# Revit family: LMNE-VL
name_source: partatom
category: Lighting Fixtures
units: mm (PartAtom-declared; Revit-internal decimal feet)

## family parameters
Always vertical = Yes
Cut with Voids When Loaded = No
Host = Ceiling
Light Source = Yes
OmniClass Number = 23.80.70.11.14
OmniClass Title = General Luminaries, Directional
Part Type = Normal
Room Calculation Point = No
Round Connector Dimension = Use Diameter
Shared = No

## types (6) — shared parameters
Assembly Code = D5020200
Color Filter = 16777215
Description = LED Magic Neutron VL
Dimming Lamp Color Temperature Shift = <None>
Housing Finish = Metal - Viscor - White
Lamp = LED
Lens Finish = Polycarbonate - Viscor - Frosted Round
Manufacturer = VISIONEERING by VISCOR
Model = LMNE
Tilt Angle = 90.00°
URL = https://www.viscor.com
Voltage = 120 V
Width = 0' - 9 1/4"

## per-type parameters (varying)
| type | Apparent Load | Emit from Line Length | Lamp Wattage | Length | Photometric Web File |
| LMNE-VL24-LED840K028LUNV | 20 VA | 1' - 11 3/8" | 20 VA | 1' - 11 3/8" | LMNE-VL24-LED840K028LUNV.IES |
| LMNE-VL48-LED840K028LUNV | 20 VA | 3' - 10 1/8" | 20 VA | 3' - 10 1/8" | LMNE-VL48-LED840K028LUNV-G001930.IES |
| LMNE-VL24-LED840K037LUNV | 28 VA | 1' - 11 3/8" | 28 VA | 1' - 11 3/8" | LMNE-VL24-LED840K037LUNV.IES |
| LMNE-VL48-LED840K037LUNV | 28 VA | 3' - 10 1/8" | 28 VA | 3' - 10 1/8" | LMNE-VL48-LED840K037LUNV-G001916.IES |
| LMNE-VL48-LED840K045LUNV | 33 VA | 3' - 10 1/8" | 33 VA | 3' - 10 1/8" | LMNE-VL48-LED840K045LUNV-G001920.IES |
| LMNE-VL48-LED840K052LUNV | 42 VA | 3' - 10 1/8" | 42 VA | 3' - 10 1/8" | LMNE-VL48-LED840K052LUNV-G001919.IES |

## geometry (parser evidence)
native form markers: Sweep x2
no freeform markers — native parametric forms only
